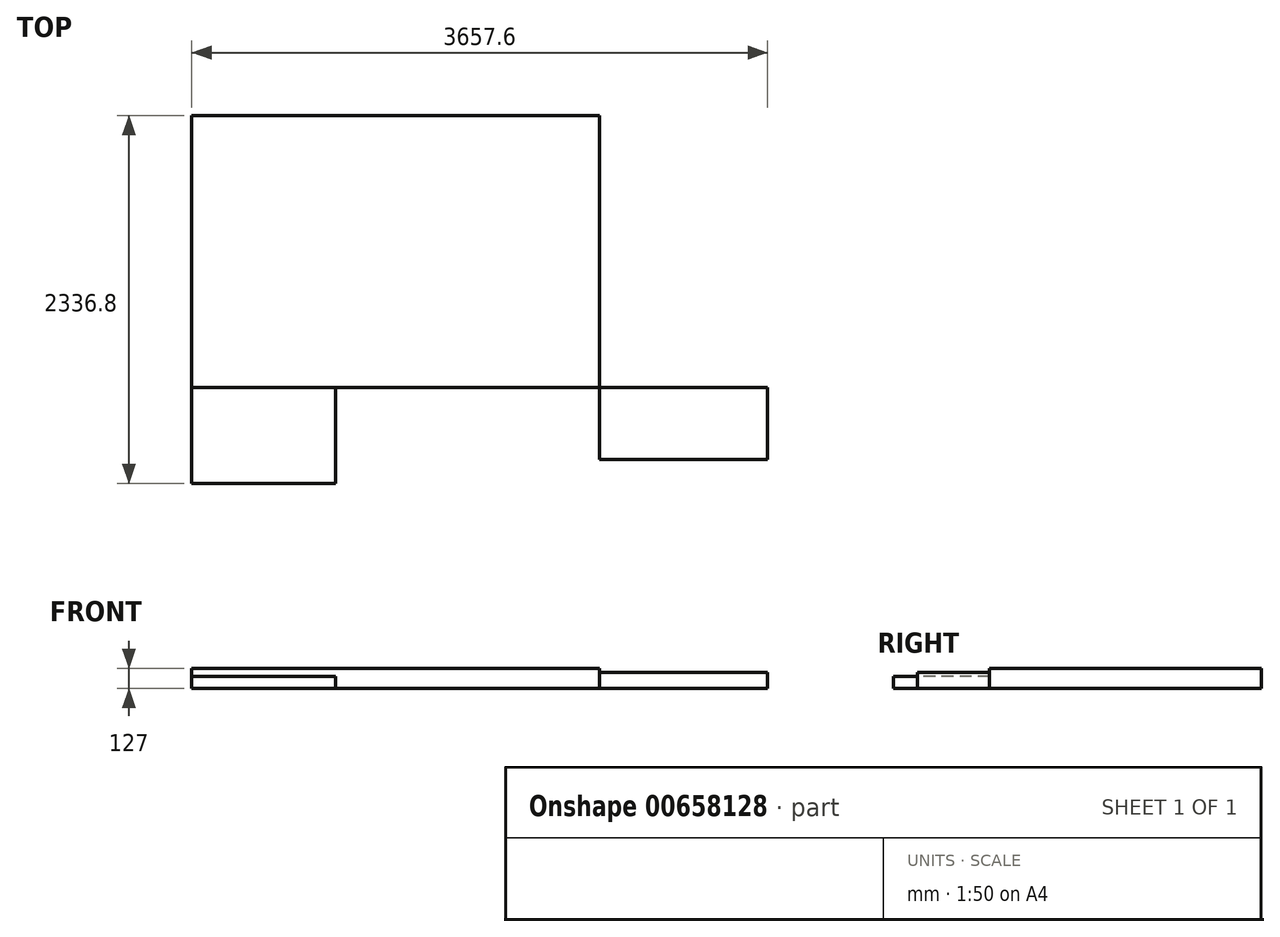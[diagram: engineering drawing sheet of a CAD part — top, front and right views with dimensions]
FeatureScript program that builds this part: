
annotation { "Feature Type Name" : "Feature", "Feature Type Description" : "" }
export const myFeature = defineFeature(function(context is Context, id is Id, definition is map)
    precondition{}
    {
        {
            var Q0;
            Q0=qCreatedBy(makeId("Top.planeOp"),FACE);
            var sketch = newSketch(context, id + "F0", { "sketchPlane" : qUnion([Q0])});
            skLineSegment(sketch, "E0.bottom", {"start": v(0, 0) * mm, "end": v(2590.8, 0) * mm});
            skLineSegment(sketch, "E0.top", {"start": v(0, 1727.2) * mm, "end": v(2590.8, 1727.2) * mm});
            skLineSegment(sketch, "E0.left", {"start": v(0, 0) * mm, "end": v(0, 1727.2) * mm});
            skLineSegment(sketch, "E0.right", {"start": v(2590.8, 0) * mm, "end": v(2590.8, 1727.2) * mm});
            skSolve(sketch);
        }
        {
            var Q0;
            Q0 = qSketchRegion(id + "F0", true);
            extrude(context, id + "F1", {"entities" : qUnion([Q0]), "depth" : 127 * mm, "offsetDistance" : 25.4 * mm});
        }
        {
            var Q0;
            Q0=makeQuery(id+"F1.opExtrude","CAP_FACE",FACE,{"disambiguationData":[OSD([sQuery(id+"F0.wireOp",EDGE,"E0.bottom"),sQuery(id+"F0.wireOp",EDGE,"E0.top"),sQuery(id+"F0.wireOp",EDGE,"E0.left"),sQuery(id+"F0.wireOp",EDGE,"E0.right")])],"isStart":false});
            var sketch = newSketch(context, id + "F2", { "sketchPlane" : qUnion([Q0])});
            skLineSegment(sketch, "E1.bottom", {"start": v(2590.8, 0) * mm, "end": v(3657.6, 0) * mm});
            skLineSegment(sketch, "E1.top", {"start": v(2590.8, -457.2) * mm, "end": v(3657.6, -457.2) * mm});
            skLineSegment(sketch, "E1.left", {"start": v(2590.8, 0) * mm, "end": v(2590.8, -457.2) * mm});
            skLineSegment(sketch, "E1.right", {"start": v(3657.6, 0) * mm, "end": v(3657.6, -457.2) * mm});
            skSolve(sketch);
        }
        {
            var Q0;
            Q0 = qSketchRegion(id + "F2", true);
            extrude(context, id + "F3", {"entities" : qUnion([Q0]), "oppositeDirection" : true, "depth" : 127 * mm, "offsetDistance" : 25.4 * mm, "hasSecondDirection" : true, "secondDirectionOppositeDirection" : true, "secondDirectionDepth" : 25.4 * mm});
        }
        {
            var Q0;
            Q0=makeQuery(id+"F1.opExtrude","CAP_FACE",FACE,{"disambiguationData":[OSD([sQuery(id+"F0.wireOp",EDGE,"E0.bottom"),sQuery(id+"F0.wireOp",EDGE,"E0.top"),sQuery(id+"F0.wireOp",EDGE,"E0.left"),sQuery(id+"F0.wireOp",EDGE,"E0.right")])],"isStart":false});
            var sketch = newSketch(context, id + "F4", { "sketchPlane" : qUnion([Q0])});
            skLineSegment(sketch, "E2.bottom", {"start": v(0, 0) * mm, "end": v(914.4, 0) * mm});
            skLineSegment(sketch, "E2.top", {"start": v(0, -609.6) * mm, "end": v(914.4, -609.6) * mm});
            skLineSegment(sketch, "E2.left", {"start": v(0, 0) * mm, "end": v(0, -609.6) * mm});
            skLineSegment(sketch, "E2.right", {"start": v(914.4, 0) * mm, "end": v(914.4, -609.6) * mm});
            skSolve(sketch);
        }
        {
            var Q0;
            Q0 = qSketchRegion(id + "F4", true);
            extrude(context, id + "F5", {"entities" : qUnion([Q0]), "oppositeDirection" : true, "depth" : 127 * mm, "offsetDistance" : 25.4 * mm, "hasSecondDirection" : true, "secondDirectionOppositeDirection" : true, "secondDirectionDepth" : 50.8 * mm});
        }
    });
